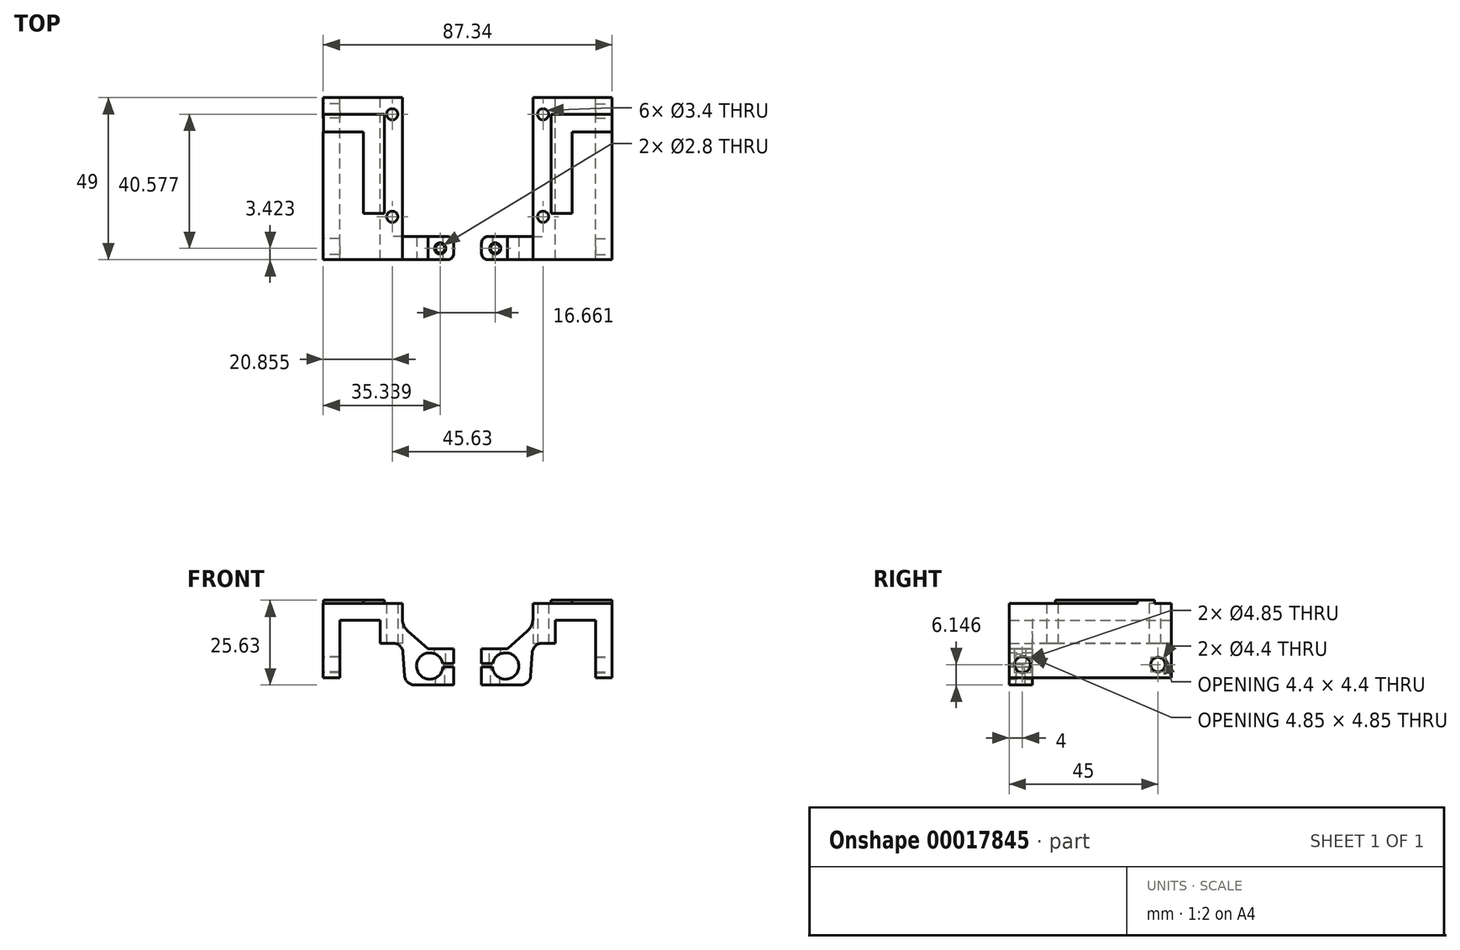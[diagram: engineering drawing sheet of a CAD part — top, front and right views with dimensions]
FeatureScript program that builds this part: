
annotation { "Feature Type Name" : "Feature", "Feature Type Description" : "" }
export const myFeature = defineFeature(function(context is Context, id is Id, definition is map)
    precondition{}
    {
        {
            var Q0;
            Q0=qCreatedBy(makeId("Front.planeOp"),FACE);
            var sketch = newSketch(context, id + "F0", { "sketchPlane" : qUnion([Q0])});
            skLineSegment(sketch, "E0", {"start": v(-18.67, 7.33) * mm, "end": v(-18.67, 29.8) * mm});
            skLineSegment(sketch, "E1", {"start": v(-18.67, 29.8) * mm, "end": v(5.26, 29.8) * mm});
            skLineSegment(sketch, "E2", {"start": v(5.26, 29.8) * mm, "end": v(5.26, 22.94) * mm});
            skLineSegment(sketch, "E3", {"start": v(-1.47, 17.8) * mm, "end": v(-1.47, 24.8) * mm});
            skLineSegment(sketch, "E4", {"start": v(-1.47, 24.8) * mm, "end": v(-13.67, 24.8) * mm});
            skLineSegment(sketch, "E5", {"start": v(-13.67, 24.8) * mm, "end": v(-13.67, 7.33) * mm});
            skLineSegment(sketch, "E6", {"start": v(-13.67, 7.33) * mm, "end": v(-18.67, 7.33) * mm});
            skLineSegment(sketch, "E7", {"start": v(5.26, 22.94) * mm, "end": v(5.26, 17.8) * mm});
            skLineSegment(sketch, "E8", {"start": v(5.26, 17.8) * mm, "end": v(-1.47, 17.8) * mm});
            skLineSegment(sketch, "E9", {"start": v(5.26, 22.94) * mm, "end": v(5.26, 22.94) * mm});
            skLineSegment(sketch, "E10", {"start": v(20.79, 16.13) * mm, "end": v(20.79, 11.7) * mm});
            skLineSegment(sketch, "E11", {"start": v(20.79, 11.7) * mm, "end": v(13.49, 11.7) * mm});
            skLineSegment(sketch, "E12", {"start": v(13.49, 11.7) * mm, "end": v(13.49, 10.67) * mm});
            skLineSegment(sketch, "E13", {"start": v(13.49, 10.67) * mm, "end": v(20.82, 10.67) * mm});
            skLineSegment(sketch, "E14", {"start": v(20.82, 10.67) * mm, "end": v(20.82, 5.18) * mm});
            skLineSegment(sketch, "E15", {"start": v(20.82, 5.18) * mm, "end": v(6.11, 5.18) * mm});
            skLineSegment(sketch, "E16", {"start": v(6.11, 5.18) * mm, "end": v(5.26, 17.8) * mm});
            skLineSegment(sketch, "E17", {"start": v(20.79, 16.13) * mm, "end": v(13, 16.13) * mm});
            skLineSegment(sketch, "E18", {"start": v(13, 16.13) * mm, "end": v(5.26, 22.94) * mm});
            skSolve(sketch);
        }
        {
            var Q0;
            Q0=makeQuery(id+"F0.imprint","IMPRINT",FACE,{"disambiguationData":[TD([[makeQuery(id+"F0.imprint","IMPRINT",EDGE,{"derivedFrom":sQuery(id+"F0.wireOp",EDGE,"E0")}),-1.0]])]});
            var Q1;
            {var subQ2=sQuery(id+"F0.wireOp",EDGE,"69cbcc5d-e0c3-48db-8baf-3487a8abab7d");Q1=makeQuery(id+"F0.imprint","IMPRINT",FACE,{"disambiguationData":[TD([[makeQuery(id+"F0.imprint","IMPRINT",EDGE,{"derivedFrom":subQ2}),-1.0]])]});}
            var Q2;
            Q2=makeQuery(id+"F0.imprint","IMPRINT",FACE,{"disambiguationData":[TD([[makeQuery(id+"F0.imprint","IMPRINT",EDGE,{"derivedFrom":sQuery(id+"F0.wireOp",EDGE,"E7")}),1.0]])]});
            extrude(context, id + "F1", {"entities" : qUnion([Q0, Q1, Q2]), "depth" : 7 * mm});
        }
        {
            var Q0;
            Q0=makeQuery(id+"F0.imprint","IMPRINT",FACE,{"disambiguationData":[TD([[makeQuery(id+"F0.imprint","IMPRINT",EDGE,{"derivedFrom":sQuery(id+"F0.wireOp",EDGE,"E0")}),-1.0]])]});
            extrude(context, id + "F2", {"entities" : qUnion([Q0]), "operationType" : NewBodyOperationType.ADD, "oppositeDirection" : true, "depth" : 42 * mm});
        }
        {
            var Q0;
            {var subQ0=sQuery(id+"F0.wireOp",EDGE,"E8");Q0=makeQuery(id+"F2.boolean.opBoolean","MERGE",FACE,{"derivedFrom":[makeQuery(id+"F1.opExtrude","SWEPT_FACE",FACE,{"disambiguationData":[OSD([subQ0])]}),makeQuery(id+"F2.opExtrude","SWEPT_FACE",FACE,{"disambiguationData":[OSD([subQ0])]})]});}
            var sketch = newSketch(context, id + "F3", { "sketchPlane" : qUnion([Q0])});
            skCircle(sketch, "E19", {"center": v(2.19, -6) * mm, "radius": 1.7 * mm});
            skCircle(sketch, "E20", {"center": v(2.19, -37) * mm, "radius": 1.7 * mm});
            skCircle(sketch, "E21", {"center": v(17.69, -21.5) * mm, "radius": 11 * mm});
            skSolve(sketch);
        }
        {
            var Q0;
            Q0=qSketchRegion(id+"F3",true);
            extrude(context, id + "F4", {"entities" : qUnion([Q0]), "operationType" : NewBodyOperationType.REMOVE, "endBound" : BoundingType.THROUGH_ALL, "oppositeDirection" : true, "depth" : 25 * mm});
        }
        {
            var Q0;
            Q0=makeQuery(id+"F1.opExtrude","CAP_FACE",FACE,{"disambiguationData":[OSD([sQuery(id+"F0.wireOp",EDGE,"E0"),sQuery(id+"F0.wireOp",EDGE,"E1"),sQuery(id+"F0.wireOp",EDGE,"E2"),sQuery(id+"F0.wireOp",EDGE,"E3"),sQuery(id+"F0.wireOp",EDGE,"E4"),sQuery(id+"F0.wireOp",EDGE,"E5"),sQuery(id+"F0.wireOp",EDGE,"E6"),sQuery(id+"F0.wireOp",EDGE,"E8"),sQuery(id+"F0.wireOp",EDGE,"E9"),sQuery(id+"F0.wireOp",EDGE,"58f11638-63e7-4b32-8aff-a1ba3c53649b"),sQuery(id+"F0.wireOp",EDGE,"E10"),sQuery(id+"F0.wireOp",EDGE,"E11"),sQuery(id+"F0.wireOp",EDGE,"E12"),sQuery(id+"F0.wireOp",EDGE,"E13"),sQuery(id+"F0.wireOp",EDGE,"E14"),sQuery(id+"F0.wireOp",EDGE,"E15"),sQuery(id+"F0.wireOp",EDGE,"E16")])],"isStart":false});
            var sketch = newSketch(context, id + "F5", { "sketchPlane" : qUnion([Q0])});
            skCircle(sketch, "E22", {"center": v(13.53, 10.9) * mm, "radius": 4 * mm});
            skSolve(sketch);
        }
        {
            var Q0;
            Q0=qSketchRegion(id+"F5",true);
            extrude(context, id + "F6", {"entities" : qUnion([Q0]), "operationType" : NewBodyOperationType.REMOVE, "oppositeDirection" : true, "depth" : 10 * mm});
        }
        {
            var Q0;
            Q0=qSketchRegion(id+"F3",true);
            extrude(context, id + "F7", {"entities" : qUnion([Q0]), "operationType" : NewBodyOperationType.REMOVE, "endBound" : BoundingType.THROUGH_ALL, "oppositeDirection" : true, "depth" : 25 * mm});
        }
        {
            var Q0;
            Q0=makeQuery(id+"F1.opExtrude","SWEPT_FACE",FACE,{"disambiguationData":[OSD([sQuery(id+"F0.wireOp",EDGE,"E17")])]});
            var sketch = newSketch(context, id + "F8", { "sketchPlane" : qUnion([Q0])});
            skCircle(sketch, "E23", {"center": v(16.67, -3.58) * mm, "radius": 1.7 * mm});
            skCircle(sketch, "E24", {"center": v(16.67, -3.58) * mm, "radius": 1.4 * mm});
            skSolve(sketch);
        }
        {
            var Q0;
            Q0=makeQuery(id+"F8.imprint","IMPRINT",FACE,{"disambiguationData":[TD([[makeQuery(id+"F8.imprint","IMPRINT",EDGE,{"derivedFrom":sQuery(id+"F8.wireOp",EDGE,"E24")}),1.0]])]});
            extrude(context, id + "F9", {"entities" : qUnion([Q0]), "operationType" : NewBodyOperationType.REMOVE, "endBound" : BoundingType.THROUGH_ALL, "oppositeDirection" : true, "depth" : 25 * mm});
        }
        {
            var Q0;
            Q0=makeQuery(id+"F8.imprint","IMPRINT",FACE,{"disambiguationData":[TD([[makeQuery(id+"F8.imprint","IMPRINT",EDGE,{"derivedFrom":sQuery(id+"F8.wireOp",EDGE,"E23")}),1.0]])]});
            extrude(context, id + "F10", {"entities" : qUnion([Q0]), "operationType" : NewBodyOperationType.REMOVE, "endBound" : BoundingType.UP_TO_NEXT, "oppositeDirection" : true, "depth" : 25 * mm});
        }
        {
            var Q0;
            Q0=makeQuery(id+"F1.opExtrude","SWEPT_EDGE",EDGE,{"disambiguationData":[OSD([sQuery(id+"F0.wireOp",EDGE,"E2"),sQuery(id+"F0.wireOp",EDGE,"E7"),sQuery(id+"F0.wireOp",EDGE,"E18")])]});
            fillet(context, id + "F11", {"entities" : qUnion([Q0]), "radius" : 5 * mm, "tangentPropagation" : true, "allowEdgeOverflow" : false});
        }
        {
            var Q0;
            Q0=makeQuery(id+"F1.opExtrude","SWEPT_EDGE",EDGE,{"disambiguationData":[OSD([sQuery(id+"F0.wireOp",EDGE,"E7"),sQuery(id+"F0.wireOp",EDGE,"E8"),sQuery(id+"F0.wireOp",EDGE,"E16")])]});
            fillet(context, id + "F12", {"entities" : qUnion([Q0]), "radius" : 3 * mm, "tangentPropagation" : true, "allowEdgeOverflow" : false});
        }
        {
            var Q0;
            Q0=makeQuery(id+"F1.opExtrude","SWEPT_EDGE",EDGE,{"disambiguationData":[OSD([sQuery(id+"F0.wireOp",EDGE,"E15"),sQuery(id+"F0.wireOp",EDGE,"E16")])]});
            fillet(context, id + "F13", {"entities" : qUnion([Q0]), "radius" : 3 * mm, "tangentPropagation" : true, "allowEdgeOverflow" : false});
        }
        {
            var Q0;
            Q0=makeQuery(id+"F1.opExtrude","CAP_EDGE",EDGE,{"disambiguationData":[OSD([sQuery(id+"F0.wireOp",EDGE,"E10")])],"isStart":false});
            var Q1;
            Q1=makeQuery(id+"F1.opExtrude","CAP_EDGE",EDGE,{"disambiguationData":[OSD([sQuery(id+"F0.wireOp",EDGE,"E14")])],"isStart":false});
            var Q2;
            Q2=makeQuery(id+"F1.opExtrude","CAP_EDGE",EDGE,{"disambiguationData":[OSD([sQuery(id+"F0.wireOp",EDGE,"E10")])],"isStart":true});
            var Q3;
            Q3=makeQuery(id+"F1.opExtrude","CAP_EDGE",EDGE,{"disambiguationData":[OSD([sQuery(id+"F0.wireOp",EDGE,"E14")])],"isStart":true});
            fillet(context, id + "F14", {"entities" : qUnion([Q0, Q1, Q2, Q3]), "radius" : 2 * mm, "tangentPropagation" : true, "allowEdgeOverflow" : false});
        }
        {
            var Q0;
            {var subQ0=sQuery(id+"F0.wireOp",EDGE,"E0");Q0=makeQuery(id+"F2.boolean.opBoolean","MERGE",FACE,{"derivedFrom":[makeQuery(id+"F1.opExtrude","SWEPT_FACE",FACE,{"disambiguationData":[OSD([subQ0])]}),makeQuery(id+"F2.opExtrude","SWEPT_FACE",FACE,{"disambiguationData":[OSD([subQ0])]})]});}
            var sketch = newSketch(context, id + "F15", { "sketchPlane" : qUnion([Q0])});
            skCircle(sketch, "E25", {"center": v(-38, 11.33) * mm, "radius": 2.2 * mm});
            skCircle(sketch, "E26", {"center": v(3, 11.33) * mm, "radius": 2.43 * mm});
            skSolve(sketch);
        }
        {
            var Q0;
            Q0=qSketchRegion(id+"F15",true);
            extrude(context, id + "F16", {"entities" : qUnion([Q0]), "operationType" : NewBodyOperationType.REMOVE, "oppositeDirection" : true, "depth" : 6 * mm});
        }
        {
            var Q0;
            {var subQ0=sQuery(id+"F0.wireOp",EDGE,"E1");Q0=makeQuery(id+"F2.boolean.opBoolean","MERGE",FACE,{"derivedFrom":[makeQuery(id+"F1.opExtrude","SWEPT_FACE",FACE,{"disambiguationData":[OSD([subQ0])]}),makeQuery(id+"F2.opExtrude","SWEPT_FACE",FACE,{"disambiguationData":[OSD([subQ0])]})]});}
            var sketch = newSketch(context, id + "F17", { "sketchPlane" : qUnion([Q0])});
            skText(sketch, "E27", { "text": "L", "fontName": "OpenSans-Bold.ttf"});
            const initialGuessF17  = {"E27": [0.0036, 0.03693, -1, 0, 0.0302]};
            skSetInitialGuess(sketch, initialGuessF17);
            skSolve(sketch);
        }
        {
            var Q0;
            Q0=qSketchRegion(id+"F17",true);
            extrude(context, id + "F18", {"entities" : qUnion([Q0]), "operationType" : NewBodyOperationType.ADD, "depth" : 1 * mm});
        }
        {
            var Q0;
            Q0=makeQuery(id+"F1.opExtrude","SWEPT_BODY",BODY,{"disambiguationData":[OSD([sQuery(id+"F0.wireOp",EDGE,"E0"),sQuery(id+"F0.wireOp",EDGE,"E1"),sQuery(id+"F0.wireOp",EDGE,"E2"),sQuery(id+"F0.wireOp",EDGE,"E3"),sQuery(id+"F0.wireOp",EDGE,"E4"),sQuery(id+"F0.wireOp",EDGE,"E5"),sQuery(id+"F0.wireOp",EDGE,"E6"),sQuery(id+"F0.wireOp",EDGE,"E8"),sQuery(id+"F0.wireOp",EDGE,"E10"),sQuery(id+"F0.wireOp",EDGE,"E11"),sQuery(id+"F0.wireOp",EDGE,"E12"),sQuery(id+"F0.wireOp",EDGE,"E13"),sQuery(id+"F0.wireOp",EDGE,"E14"),sQuery(id+"F0.wireOp",EDGE,"E15"),sQuery(id+"F0.wireOp",EDGE,"E16"),sQuery(id+"F0.wireOp",EDGE,"E17"),sQuery(id+"F0.wireOp",EDGE,"E18")])]});
            var Q1;
            Q1=qCreatedBy(makeId("Right.planeOp"),FACE);
            mirror(context, id + "F19", {"entities" : qUnion([Q0]), "mirrorPlane" : qUnion([Q1])});
        }
        {
            var Q0;
            Q0=makeQuery(id+"F19.opPattern","COPY",BODY,{"derivedFrom":makeQuery(id+"F1.opExtrude","SWEPT_BODY",BODY,{"disambiguationData":[OSD([sQuery(id+"F0.wireOp",EDGE,"E0"),sQuery(id+"F0.wireOp",EDGE,"E1"),sQuery(id+"F0.wireOp",EDGE,"E2"),sQuery(id+"F0.wireOp",EDGE,"E3"),sQuery(id+"F0.wireOp",EDGE,"E4"),sQuery(id+"F0.wireOp",EDGE,"E5"),sQuery(id+"F0.wireOp",EDGE,"E6"),sQuery(id+"F0.wireOp",EDGE,"E8"),sQuery(id+"F0.wireOp",EDGE,"E10"),sQuery(id+"F0.wireOp",EDGE,"E11"),sQuery(id+"F0.wireOp",EDGE,"E12"),sQuery(id+"F0.wireOp",EDGE,"E13"),sQuery(id+"F0.wireOp",EDGE,"E14"),sQuery(id+"F0.wireOp",EDGE,"E15"),sQuery(id+"F0.wireOp",EDGE,"E16"),sQuery(id+"F0.wireOp",EDGE,"E17"),sQuery(id+"F0.wireOp",EDGE,"E18")])]}),"instanceName":"1"});
            transform(context, id + "F20", {"entities" : qUnion([Q0]), "transformType" : TransformType.TRANSLATION_3D, "dx" : 50 * mm, "dy" : 0 * mm, "dz" : 0 * mm, "makeCopy" : false});
        }
    });
